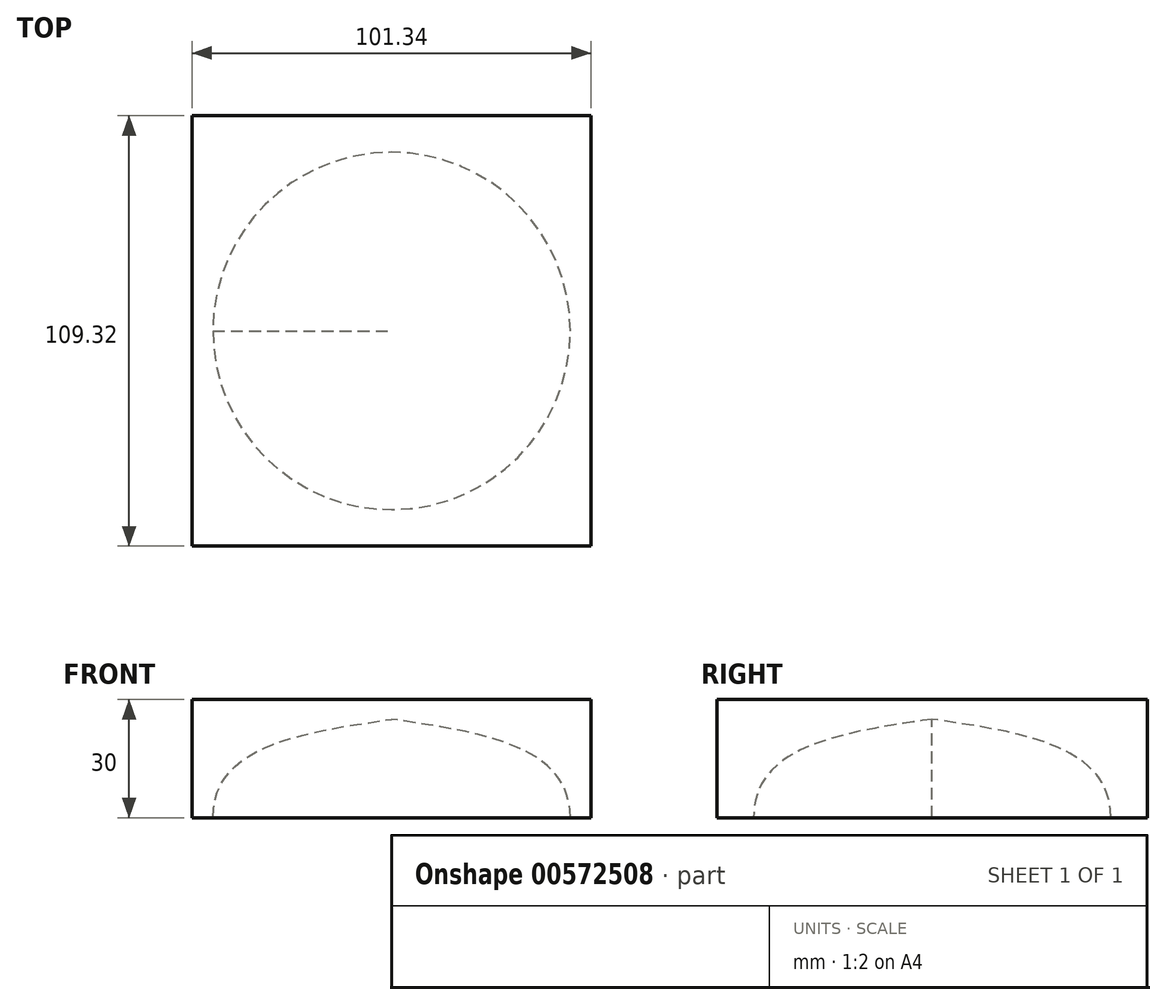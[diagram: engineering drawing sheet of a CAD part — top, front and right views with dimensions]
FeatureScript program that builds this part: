
annotation { "Feature Type Name" : "Feature", "Feature Type Description" : "" }
export const myFeature = defineFeature(function(context is Context, id is Id, definition is map)
    precondition{}
    {
        {
            var Q0;
            Q0=qCreatedBy(makeId("Top.planeOp"),FACE);
            cPlane(context, id + "F0", {"entities" : qUnion([Q0]), "cplaneType" : CPlaneType.OFFSET, "offset" : 25 * mm, "oppositeDirection" : true, "width" : 150 * mm, "height" : 150 * mm});
        }
        {
            var Q0;
            Q0=qCreatedBy(id+"F0.planeOp",FACE);
            var sketch = newSketch(context, id + "F1", { "sketchPlane" : qUnion([Q0])});
            skPoint(sketch, "E0", {"position": v(0, 0) * mm});
            skCircle(sketch, "E1", {"center": v(0, 0) * mm, "radius": 45.4 * mm});
            skLineSegment(sketch, "E2.bottom", {"start": v(50.67, 54.66) * mm, "end": v(-50.67, 54.66) * mm});
            skLineSegment(sketch, "E2.top", {"start": v(50.67, -54.66) * mm, "end": v(-50.67, -54.66) * mm});
            skLineSegment(sketch, "E2.left", {"start": v(50.67, 54.66) * mm, "end": v(50.67, -54.66) * mm});
            skLineSegment(sketch, "E2.right", {"start": v(-50.67, 54.66) * mm, "end": v(-50.67, -54.66) * mm});
            skSolve(sketch);
        }
        {
            var Q0;
            Q0=makeQuery(id+"F1.imprint","IMPRINT",FACE,{"disambiguationData":[TD([[makeQuery(id+"F1.imprint","IMPRINT",EDGE,{"derivedFrom":sQuery(id+"F1.wireOp",EDGE,"E1")}),-1.0]])]});
            var Q1;
            Q1=makeQuery(id+"F1.imprint","IMPRINT",FACE,{"disambiguationData":[TD([[makeQuery(id+"F1.imprint","IMPRINT",EDGE,{"derivedFrom":sQuery(id+"F1.wireOp",EDGE,"E1")}),1.0]])]});
            extrude(context, id + "F2", {"entities" : qUnion([Q0, Q1]), "depth" : 30 * mm, "offsetDistance" : 25 * mm});
        }
        {
            var Q0;
            Q0=makeQuery(id+"F1.imprint","IMPRINT",FACE,{"disambiguationData":[TD([[makeQuery(id+"F1.imprint","IMPRINT",EDGE,{"derivedFrom":sQuery(id+"F1.wireOp",EDGE,"E1")}),1.0]])]});
            var Q1;
            Q1=qCreatedBy(makeId("Origin.pointOp"),VERTEX);
            loft(context, id + "F3", {"operationType" : NewBodyOperationType.REMOVE, "startCondition" : LoftEndDerivativeType.NORMAL_TO_PROFILE, "startMagnitude" : 2, "sheetProfilesArray" : [{ "sheetProfileEntities" : qUnion([Q0]) }, { "sheetProfileEntities" : qUnion([Q1]) }]});
        }
    });
